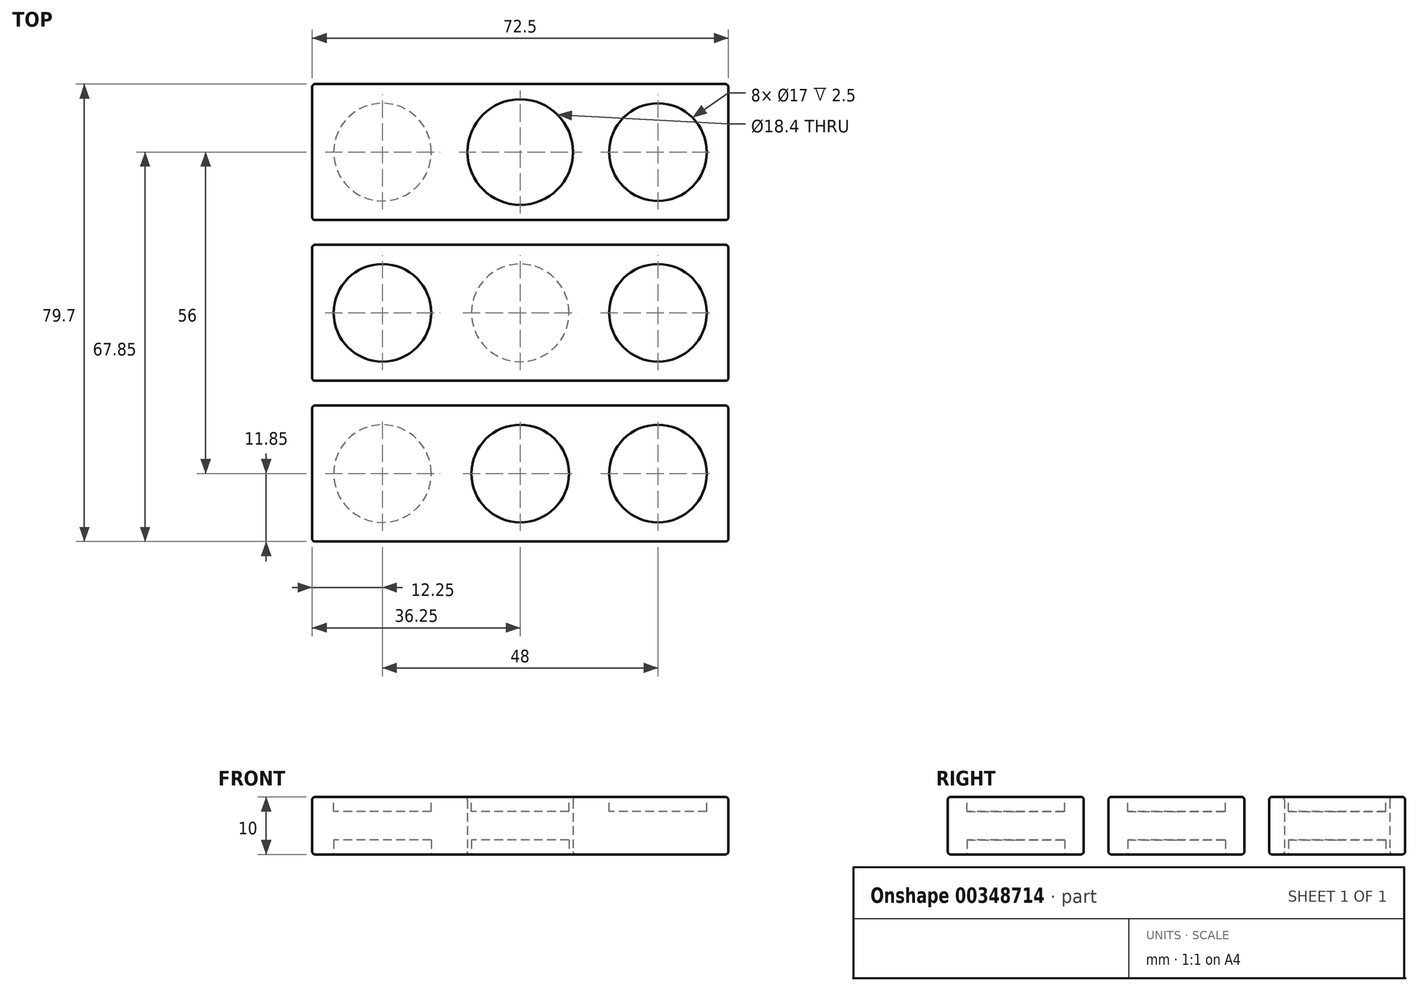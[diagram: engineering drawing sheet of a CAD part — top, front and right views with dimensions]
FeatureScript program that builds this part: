
annotation { "Feature Type Name" : "Feature", "Feature Type Description" : "" }
export const myFeature = defineFeature(function(context is Context, id is Id, definition is map)
    precondition{}
    {
        {
            var Q0;
            Q0=qCreatedBy(makeId("Top.planeOp"),FACE);
            var sketch = newSketch(context, id + "F0", { "sketchPlane" : qUnion([Q0])});
            skLineSegment(sketch, "E0", {"start": v(0, 0) * mm, "end": v(0, -99.1) * mm, "construction": true});
            skLineSegment(sketch, "E1.bottom", {"start": v(0, 0) * mm, "end": v(72.5, 0) * mm});
            skLineSegment(sketch, "E1.top", {"start": v(0, -23.7) * mm, "end": v(72.5, -23.7) * mm});
            skLineSegment(sketch, "E1.left", {"start": v(0, 0) * mm, "end": v(0, -23.7) * mm});
            skLineSegment(sketch, "E1.right", {"start": v(72.5, 0) * mm, "end": v(72.5, -23.7) * mm});
            skLineSegment(sketch, "E2.0.1.0", {"start": v(72.5, -28) * mm, "end": v(72.5, -51.7) * mm});
            skLineSegment(sketch, "E2.0.1.1", {"start": v(0, -51.7) * mm, "end": v(72.5, -51.7) * mm});
            skLineSegment(sketch, "E2.0.1.2", {"start": v(0, -28) * mm, "end": v(72.5, -28) * mm});
            skLineSegment(sketch, "E2.0.1.3", {"start": v(0, -28) * mm, "end": v(0, -51.7) * mm});
            skLineSegment(sketch, "E2.0.2.0", {"start": v(72.5, -56) * mm, "end": v(72.5, -79.7) * mm});
            skLineSegment(sketch, "E2.0.2.1", {"start": v(0, -79.7) * mm, "end": v(72.5, -79.7) * mm});
            skLineSegment(sketch, "E2.0.2.2", {"start": v(0, -56) * mm, "end": v(72.5, -56) * mm});
            skLineSegment(sketch, "E2.0.2.3", {"start": v(0, -56) * mm, "end": v(0, -79.7) * mm});
            skLineSegment(sketch, "E2.0.3.0", {"start": v(72.5, -84) * mm, "end": v(72.5, -107.7) * mm});
            skLineSegment(sketch, "E2.0.3.1", {"start": v(0, -107.7) * mm, "end": v(72.5, -107.7) * mm});
            skLineSegment(sketch, "E2.0.3.2", {"start": v(0, -84) * mm, "end": v(72.5, -84) * mm});
            skLineSegment(sketch, "E2.0.3.3", {"start": v(0, -84) * mm, "end": v(0, -107.7) * mm});
            skLineSegment(sketch, "E2.0.4.0", {"start": v(72.5, -112) * mm, "end": v(72.5, -135.7) * mm});
            skLineSegment(sketch, "E2.0.4.1", {"start": v(0, -135.7) * mm, "end": v(72.5, -135.7) * mm});
            skLineSegment(sketch, "E2.0.4.2", {"start": v(0, -112) * mm, "end": v(72.5, -112) * mm});
            skLineSegment(sketch, "E2.0.4.3", {"start": v(0, -112) * mm, "end": v(0, -135.7) * mm});
            skLineSegment(sketch, "E2.0.5.0", {"start": v(72.5, -140) * mm, "end": v(72.5, -163.7) * mm});
            skLineSegment(sketch, "E2.0.5.1", {"start": v(0, -163.7) * mm, "end": v(72.5, -163.7) * mm});
            skLineSegment(sketch, "E2.0.5.2", {"start": v(0, -140) * mm, "end": v(72.5, -140) * mm});
            skLineSegment(sketch, "E2.0.5.3", {"start": v(0, -140) * mm, "end": v(0, -163.7) * mm});
            skLineSegment(sketch, "E2.direction1", {"start": v(72.5, -23.7) * mm, "end": v(97.83, -23.7) * mm, "construction": true});
            skLineSegment(sketch, "E2.direction2", {"start": v(72.5, -23.7) * mm, "end": v(72.5, -51.7) * mm, "construction": true});
            skLineSegment(sketch, "E3", {"start": v(0, -11.85) * mm, "end": v(12.25, -11.85) * mm, "construction": true});
            skLineSegment(sketch, "E4", {"start": v(12.25, -11.85) * mm, "end": v(36.25, -11.85) * mm, "construction": true});
            skLineSegment(sketch, "E5", {"start": v(36.25, -11.85) * mm, "end": v(60.25, -11.85) * mm, "construction": true});
            skLineSegment(sketch, "E6", {"start": v(60.25, -11.85) * mm, "end": v(72.5, -11.85) * mm, "construction": true});
            skLineSegment(sketch, "E7", {"start": v(12.25, -11.85) * mm, "end": v(12.25, -182.05) * mm, "construction": true});
            skLineSegment(sketch, "E8", {"start": v(36.25, -11.85) * mm, "end": v(36.25, -186.32) * mm, "construction": true});
            skLineSegment(sketch, "E9", {"start": v(60.25, -11.85) * mm, "end": v(60.25, -189.7) * mm, "construction": true});
            skCircle(sketch, "E10", {"center": v(12.25, -11.85) * mm, "radius": 9.2 * mm});
            skCircle(sketch, "E11", {"center": v(36.25, -11.85) * mm, "radius": 9.2 * mm});
            skLineSegment(sketch, "E12", {"start": v(0, -39.85) * mm, "end": v(72.5, -39.85) * mm, "construction": true});
            skLineSegment(sketch, "E13", {"start": v(0, -67.85) * mm, "end": v(72.5, -67.85) * mm, "construction": true});
            skLineSegment(sketch, "E14", {"start": v(0, -95.85) * mm, "end": v(72.5, -95.85) * mm, "construction": true});
            skLineSegment(sketch, "E15", {"start": v(0, -123.85) * mm, "end": v(72.5, -123.85) * mm, "construction": true});
            skLineSegment(sketch, "E16", {"start": v(0, -151.85) * mm, "end": v(72.5, -151.85) * mm, "construction": true});
            skCircle(sketch, "E17", {"center": v(12.25, -39.85) * mm, "radius": 9.2 * mm});
            skCircle(sketch, "E18", {"center": v(12.25, -67.85) * mm, "radius": 9.2 * mm});
            skCircle(sketch, "E19", {"center": v(36.25, -95.85) * mm, "radius": 9.2 * mm});
            skCircle(sketch, "E20", {"center": v(36.25, -39.85) * mm, "radius": 8.5 * mm});
            skCircle(sketch, "E21", {"center": v(36.25, -67.85) * mm, "radius": 8.5 * mm});
            skCircle(sketch, "E22", {"center": v(12.25, -95.85) * mm, "radius": 8.5 * mm});
            skCircle(sketch, "E23", {"center": v(36.25, -123.85) * mm, "radius": 8.5 * mm});
            skCircle(sketch, "E24", {"center": v(12.25, -151.85) * mm, "radius": 8.5 * mm});
            skSolve(sketch);
        }
        {
            var Q0;
            Q0=makeQuery(id+"F0.imprint","IMPRINT",FACE,{"disambiguationData":[TD([[makeQuery(id+"F0.imprint","IMPRINT",EDGE,{"derivedFrom":sQuery(id+"F0.wireOp",EDGE,"E1.bottom")}),-1.0]])]});
            var Q1;
            Q1=makeQuery(id+"F0.imprint","IMPRINT",FACE,{"disambiguationData":[TD([[makeQuery(id+"F0.imprint","IMPRINT",EDGE,{"derivedFrom":sQuery(id+"F0.wireOp",EDGE,"E2.0.1.0")}),-1.0]])]});
            var Q2;
            Q2=makeQuery(id+"F0.imprint","IMPRINT",FACE,{"disambiguationData":[TD([[makeQuery(id+"F0.imprint","IMPRINT",EDGE,{"derivedFrom":sQuery(id+"F0.wireOp",EDGE,"E2.0.2.0")}),-1.0]])]});
            var Q3;
            Q3=makeQuery(id+"F0.imprint","IMPRINT",FACE,{"disambiguationData":[TD([[makeQuery(id+"F0.imprint","IMPRINT",EDGE,{"derivedFrom":sQuery(id+"F0.wireOp",EDGE,"E2.0.3.0")}),-1.0]])]});
            var Q4;
            Q4=makeQuery(id+"F0.imprint","IMPRINT",FACE,{"disambiguationData":[TD([[makeQuery(id+"F0.imprint","IMPRINT",EDGE,{"derivedFrom":sQuery(id+"F0.wireOp",EDGE,"E2.0.4.0")}),-1.0]])]});
            var Q5;
            Q5=makeQuery(id+"F0.imprint","IMPRINT",FACE,{"disambiguationData":[TD([[makeQuery(id+"F0.imprint","IMPRINT",EDGE,{"derivedFrom":sQuery(id+"F0.wireOp",EDGE,"E2.0.5.0")}),-1.0]])]});
            var Q6;
            Q6=makeQuery(id+"F0.imprint","IMPRINT",FACE,{"disambiguationData":[TD([[makeQuery(id+"F0.imprint","IMPRINT",EDGE,{"derivedFrom":sQuery(id+"F0.wireOp",EDGE,"E23")}),1.0]])]});
            var Q7;
            Q7=makeQuery(id+"F0.imprint","IMPRINT",FACE,{"disambiguationData":[TD([[makeQuery(id+"F0.imprint","IMPRINT",EDGE,{"derivedFrom":sQuery(id+"F0.wireOp",EDGE,"E24")}),1.0]])]});
            var Q8;
            Q8=makeQuery(id+"F0.imprint","IMPRINT",FACE,{"disambiguationData":[TD([[makeQuery(id+"F0.imprint","IMPRINT",EDGE,{"derivedFrom":sQuery(id+"F0.wireOp",EDGE,"E21")}),1.0]])]});
            var Q9;
            Q9=makeQuery(id+"F0.imprint","IMPRINT",FACE,{"disambiguationData":[TD([[makeQuery(id+"F0.imprint","IMPRINT",EDGE,{"derivedFrom":sQuery(id+"F0.wireOp",EDGE,"E20")}),1.0]])]});
            var Q10;
            Q10=makeQuery(id+"F0.imprint","IMPRINT",FACE,{"disambiguationData":[TD([[makeQuery(id+"F0.imprint","IMPRINT",EDGE,{"derivedFrom":sQuery(id+"F0.wireOp",EDGE,"E22")}),1.0]])]});
            extrude(context, id + "F1", {"entities" : qUnion([Q0, Q1, Q2, Q3, Q4, Q5, Q6, Q7, Q8, Q9, Q10]), "depth" : 10 * mm});
        }
        {
            var Q0;
            Q0=makeQuery(id+"F0.imprint","IMPRINT",FACE,{"disambiguationData":[TD([[makeQuery(id+"F0.imprint","IMPRINT",EDGE,{"derivedFrom":sQuery(id+"F0.wireOp",EDGE,"E24")}),1.0]])]});
            var Q1;
            Q1=makeQuery(id+"F0.imprint","IMPRINT",FACE,{"disambiguationData":[TD([[makeQuery(id+"F0.imprint","IMPRINT",EDGE,{"derivedFrom":sQuery(id+"F0.wireOp",EDGE,"E23")}),1.0]])]});
            var Q2;
            Q2=makeQuery(id+"F0.imprint","IMPRINT",FACE,{"disambiguationData":[TD([[makeQuery(id+"F0.imprint","IMPRINT",EDGE,{"derivedFrom":sQuery(id+"F0.wireOp",EDGE,"E22")}),1.0]])]});
            var Q3;
            Q3=makeQuery(id+"F0.imprint","IMPRINT",FACE,{"disambiguationData":[TD([[makeQuery(id+"F0.imprint","IMPRINT",EDGE,{"derivedFrom":sQuery(id+"F0.wireOp",EDGE,"E21")}),1.0]])]});
            var Q4;
            Q4=makeQuery(id+"F0.imprint","IMPRINT",FACE,{"disambiguationData":[TD([[makeQuery(id+"F0.imprint","IMPRINT",EDGE,{"derivedFrom":sQuery(id+"F0.wireOp",EDGE,"E20")}),1.0]])]});
            extrude(context, id + "F2", {"entities" : qUnion([Q0, Q1, Q2, Q3, Q4]), "operationType" : NewBodyOperationType.REMOVE, "depth" : 2.5 * mm});
        }
        {
            var Q0;
            Q0=makeQuery(id+"F1.opExtrude","CAP_FACE",FACE,{"disambiguationData":[OSD([sQuery(id+"F0.wireOp",EDGE,"E2.0.5.0"),sQuery(id+"F0.wireOp",EDGE,"E2.0.5.1"),sQuery(id+"F0.wireOp",EDGE,"E2.0.5.2"),sQuery(id+"F0.wireOp",EDGE,"E2.0.5.3")])],"isStart":false});
            var sketch = newSketch(context, id + "F3", { "sketchPlane" : qUnion([Q0])});
            skCircle(sketch, "E25", {"center": v(60.25, -11.85) * mm, "radius": 8.5 * mm});
            skCircle(sketch, "E26", {"center": v(60.25, -39.85) * mm, "radius": 8.5 * mm});
            skCircle(sketch, "E27", {"center": v(60.25, -67.85) * mm, "radius": 8.5 * mm});
            skCircle(sketch, "E28", {"center": v(60.25, -95.85) * mm, "radius": 8.5 * mm});
            skCircle(sketch, "E29", {"center": v(60.25, -123.85) * mm, "radius": 8.5 * mm});
            skCircle(sketch, "E30", {"center": v(12.25, -123.85) * mm, "radius": 8.5 * mm});
            skCircle(sketch, "E31", {"center": v(36.25, -151.85) * mm, "radius": 8.5 * mm});
            skCircle(sketch, "E32", {"center": v(60.25, -151.85) * mm, "radius": 8.5 * mm});
            skLineSegment(sketch, "E33", {"start": v(36.25, -163.7) * mm, "end": v(36.25, 0) * mm, "construction": true});
            skPoint(sketch, "E34.startSnap0", {"position": v(0, -151.85) * mm});
            skLineSegment(sketch, "E35", {"start": v(0, -151.85) * mm, "end": v(0, -125.8) * mm, "construction": true});
            skLineSegment(sketch, "E36", {"start": v(0, -151.85) * mm, "end": v(12.25, -151.85) * mm, "construction": true});
            skLineSegment(sketch, "E37", {"start": v(12.25, -151.85) * mm, "end": v(36.25, -151.85) * mm, "construction": true});
            skLineSegment(sketch, "E38", {"start": v(36.25, -151.85) * mm, "end": v(60.25, -151.85) * mm, "construction": true});
            skLineSegment(sketch, "E39", {"start": v(60.25, -151.85) * mm, "end": v(72.5, -151.85) * mm, "construction": true});
            skLineSegment(sketch, "E40.0.1.0", {"start": v(0, -123.85) * mm, "end": v(12.25, -123.85) * mm, "construction": true});
            skLineSegment(sketch, "E40.0.1.1", {"start": v(12.25, -123.85) * mm, "end": v(36.25, -123.85) * mm, "construction": true});
            skLineSegment(sketch, "E40.0.1.2", {"start": v(36.25, -123.85) * mm, "end": v(60.25, -123.85) * mm, "construction": true});
            skLineSegment(sketch, "E40.0.1.3", {"start": v(60.25, -123.85) * mm, "end": v(72.5, -123.85) * mm, "construction": true});
            skLineSegment(sketch, "E40.0.2.0", {"start": v(0, -95.85) * mm, "end": v(12.25, -95.85) * mm, "construction": true});
            skLineSegment(sketch, "E40.0.2.1", {"start": v(12.25, -95.85) * mm, "end": v(36.25, -95.85) * mm, "construction": true});
            skLineSegment(sketch, "E40.0.2.2", {"start": v(36.25, -95.85) * mm, "end": v(60.25, -95.85) * mm, "construction": true});
            skLineSegment(sketch, "E40.0.2.3", {"start": v(60.25, -95.85) * mm, "end": v(72.5, -95.85) * mm, "construction": true});
            skLineSegment(sketch, "E40.0.3.0", {"start": v(0, -67.85) * mm, "end": v(12.25, -67.85) * mm, "construction": true});
            skLineSegment(sketch, "E40.0.3.1", {"start": v(12.25, -67.85) * mm, "end": v(36.25, -67.85) * mm, "construction": true});
            skLineSegment(sketch, "E40.0.3.2", {"start": v(36.25, -67.85) * mm, "end": v(60.25, -67.85) * mm, "construction": true});
            skLineSegment(sketch, "E40.0.3.3", {"start": v(60.25, -67.85) * mm, "end": v(72.5, -67.85) * mm, "construction": true});
            skLineSegment(sketch, "E40.0.4.0", {"start": v(0, -39.85) * mm, "end": v(12.25, -39.85) * mm, "construction": true});
            skLineSegment(sketch, "E40.0.4.1", {"start": v(12.25, -39.85) * mm, "end": v(36.25, -39.85) * mm, "construction": true});
            skLineSegment(sketch, "E40.0.4.2", {"start": v(36.25, -39.85) * mm, "end": v(60.25, -39.85) * mm, "construction": true});
            skLineSegment(sketch, "E40.0.4.3", {"start": v(60.25, -39.85) * mm, "end": v(72.5, -39.85) * mm, "construction": true});
            skLineSegment(sketch, "E40.0.5.0", {"start": v(0, -11.85) * mm, "end": v(12.25, -11.85) * mm, "construction": true});
            skLineSegment(sketch, "E40.0.5.1", {"start": v(12.25, -11.85) * mm, "end": v(36.25, -11.85) * mm, "construction": true});
            skLineSegment(sketch, "E40.0.5.2", {"start": v(36.25, -11.85) * mm, "end": v(60.25, -11.85) * mm, "construction": true});
            skLineSegment(sketch, "E40.0.5.3", {"start": v(60.25, -11.85) * mm, "end": v(72.5, -11.85) * mm, "construction": true});
            skLineSegment(sketch, "E40.direction1", {"start": v(0, -151.85) * mm, "end": v(25, -151.85) * mm, "construction": true});
            skLineSegment(sketch, "E40.direction2", {"start": v(0, -151.85) * mm, "end": v(0, -123.85) * mm, "construction": true});
            skSolve(sketch);
        }
        {
            var Q0;
            Q0=makeQuery(id+"F3.imprint","IMPRINT",FACE,{"disambiguationData":[TD([[makeQuery(id+"F3.imprint","IMPRINT",EDGE,{"derivedFrom":sQuery(id+"F3.wireOp",EDGE,"E30")}),1.0]])]});
            var Q1;
            Q1=makeQuery(id+"F3.imprint","IMPRINT",FACE,{"disambiguationData":[TD([[makeQuery(id+"F3.imprint","IMPRINT",EDGE,{"derivedFrom":sQuery(id+"F3.wireOp",EDGE,"E31")}),1.0]])]});
            var Q2;
            Q2=makeQuery(id+"F3.imprint","IMPRINT",FACE,{"disambiguationData":[TD([[makeQuery(id+"F3.imprint","IMPRINT",EDGE,{"derivedFrom":sQuery(id+"F3.wireOp",EDGE,"E32")}),1.0]])]});
            var Q3;
            Q3=makeQuery(id+"F3.imprint","IMPRINT",FACE,{"disambiguationData":[TD([[makeQuery(id+"F3.imprint","IMPRINT",EDGE,{"derivedFrom":sQuery(id+"F3.wireOp",EDGE,"E29")}),1.0]])]});
            var Q4;
            Q4=makeQuery(id+"F3.imprint","IMPRINT",FACE,{"disambiguationData":[TD([[makeQuery(id+"F3.imprint","IMPRINT",EDGE,{"derivedFrom":sQuery(id+"F3.wireOp",EDGE,"E28")}),1.0]])]});
            var Q5;
            Q5=makeQuery(id+"F3.imprint","IMPRINT",FACE,{"disambiguationData":[TD([[makeQuery(id+"F3.imprint","IMPRINT",EDGE,{"derivedFrom":sQuery(id+"F3.wireOp",EDGE,"E27")}),1.0]])]});
            var Q6;
            Q6=makeQuery(id+"F3.imprint","IMPRINT",FACE,{"disambiguationData":[TD([[makeQuery(id+"F3.imprint","IMPRINT",EDGE,{"derivedFrom":sQuery(id+"F3.wireOp",EDGE,"E26")}),1.0]])]});
            var Q7;
            Q7=makeQuery(id+"F3.imprint","IMPRINT",FACE,{"disambiguationData":[TD([[makeQuery(id+"F3.imprint","IMPRINT",EDGE,{"derivedFrom":sQuery(id+"F3.wireOp",EDGE,"E25")}),1.0]])]});
            extrude(context, id + "F4", {"entities" : qUnion([Q0, Q1, Q2, Q3, Q4, Q5, Q6, Q7]), "operationType" : NewBodyOperationType.REMOVE, "oppositeDirection" : true, "depth" : 2.5 * mm});
        }
        {
            var Q0;
            Q0=makeQuery(id+"F1.opExtrude","SWEPT_FACE",FACE,{"disambiguationData":[OSD([sQuery(id+"F0.wireOp",EDGE,"E2.0.5.1")])]});
            var Q1;
            Q1=makeQuery(id+"F1.opExtrude","SWEPT_FACE",FACE,{"disambiguationData":[OSD([sQuery(id+"F0.wireOp",EDGE,"E2.0.5.0")])]});
            var Q2;
            Q2=makeQuery(id+"F1.opExtrude","SWEPT_FACE",FACE,{"disambiguationData":[OSD([sQuery(id+"F0.wireOp",EDGE,"E2.0.4.0")])]});
            var Q3;
            Q3=makeQuery(id+"F1.opExtrude","SWEPT_FACE",FACE,{"disambiguationData":[OSD([sQuery(id+"F0.wireOp",EDGE,"E2.0.3.0")])]});
            var Q4;
            Q4=makeQuery(id+"F1.opExtrude","SWEPT_FACE",FACE,{"disambiguationData":[OSD([sQuery(id+"F0.wireOp",EDGE,"E2.0.2.0")])]});
            var Q5;
            Q5=makeQuery(id+"F1.opExtrude","SWEPT_FACE",FACE,{"disambiguationData":[OSD([sQuery(id+"F0.wireOp",EDGE,"E2.0.1.0")])]});
            var Q6;
            Q6=makeQuery(id+"F1.opExtrude","SWEPT_FACE",FACE,{"disambiguationData":[OSD([sQuery(id+"F0.wireOp",EDGE,"E1.right")])]});
            var Q7;
            Q7=makeQuery(id+"F1.opExtrude","SWEPT_FACE",FACE,{"disambiguationData":[OSD([sQuery(id+"F0.wireOp",EDGE,"E1.bottom")])]});
            var Q8;
            Q8=makeQuery(id+"F1.opExtrude","SWEPT_FACE",FACE,{"disambiguationData":[OSD([sQuery(id+"F0.wireOp",EDGE,"E1.left")])]});
            var Q9;
            Q9=makeQuery(id+"F1.opExtrude","SWEPT_FACE",FACE,{"disambiguationData":[OSD([sQuery(id+"F0.wireOp",EDGE,"E2.0.1.3")])]});
            var Q10;
            Q10=makeQuery(id+"F1.opExtrude","SWEPT_FACE",FACE,{"disambiguationData":[OSD([sQuery(id+"F0.wireOp",EDGE,"E2.0.2.3")])]});
            var Q11;
            Q11=makeQuery(id+"F1.opExtrude","SWEPT_FACE",FACE,{"disambiguationData":[OSD([sQuery(id+"F0.wireOp",EDGE,"E2.0.3.3")])]});
            var Q12;
            Q12=makeQuery(id+"F1.opExtrude","SWEPT_FACE",FACE,{"disambiguationData":[OSD([sQuery(id+"F0.wireOp",EDGE,"E2.0.4.3")])]});
            var Q13;
            Q13=makeQuery(id+"F1.opExtrude","SWEPT_FACE",FACE,{"disambiguationData":[OSD([sQuery(id+"F0.wireOp",EDGE,"E2.0.5.3")])]});
            var Q14;
            Q14=makeQuery(id+"F1.opExtrude","SWEPT_FACE",FACE,{"disambiguationData":[OSD([sQuery(id+"F0.wireOp",EDGE,"E2.0.5.2")])]});
            var Q15;
            Q15=makeQuery(id+"F1.opExtrude","SWEPT_FACE",FACE,{"disambiguationData":[OSD([sQuery(id+"F0.wireOp",EDGE,"E2.0.4.2")])]});
            var Q16;
            Q16=makeQuery(id+"F1.opExtrude","SWEPT_FACE",FACE,{"disambiguationData":[OSD([sQuery(id+"F0.wireOp",EDGE,"E2.0.3.2")])]});
            var Q17;
            Q17=makeQuery(id+"F1.opExtrude","SWEPT_FACE",FACE,{"disambiguationData":[OSD([sQuery(id+"F0.wireOp",EDGE,"E2.0.2.2")])]});
            var Q18;
            Q18=makeQuery(id+"F1.opExtrude","SWEPT_FACE",FACE,{"disambiguationData":[OSD([sQuery(id+"F0.wireOp",EDGE,"E2.0.1.2")])]});
            var Q19;
            Q19=makeQuery(id+"F1.opExtrude","SWEPT_FACE",FACE,{"disambiguationData":[OSD([sQuery(id+"F0.wireOp",EDGE,"E1.top")])]});
            var Q20;
            Q20=makeQuery(id+"F1.opExtrude","SWEPT_FACE",FACE,{"disambiguationData":[OSD([sQuery(id+"F0.wireOp",EDGE,"E2.0.1.1")])]});
            var Q21;
            Q21=makeQuery(id+"F1.opExtrude","SWEPT_FACE",FACE,{"disambiguationData":[OSD([sQuery(id+"F0.wireOp",EDGE,"E2.0.2.1")])]});
            var Q22;
            Q22=makeQuery(id+"F1.opExtrude","SWEPT_FACE",FACE,{"disambiguationData":[OSD([sQuery(id+"F0.wireOp",EDGE,"E2.0.3.1")])]});
            var Q23;
            Q23=makeQuery(id+"F1.opExtrude","SWEPT_FACE",FACE,{"disambiguationData":[OSD([sQuery(id+"F0.wireOp",EDGE,"E2.0.4.1")])]});
            fillet(context, id + "F5", {"entities" : qUnion([Q0, Q1, Q2, Q3, Q4, Q5, Q6, Q7, Q8, Q9, Q10, Q11, Q12, Q13, Q14, Q15, Q16, Q17, Q18, Q19, Q20, Q21, Q22, Q23]), "radius" : 0.5 * mm, "tangentPropagation" : true, "allowEdgeOverflow" : false});
        }
        {
            var Q0;
            Q0=makeQuery(id+"F1.opExtrude","SWEPT_FACE",FACE,{"disambiguationData":[OSD([sQuery(id+"F0.wireOp",EDGE,"E17")])]});
            var Q1;
            Q1=makeQuery(id+"F1.opExtrude","SWEPT_FACE",FACE,{"disambiguationData":[OSD([sQuery(id+"F0.wireOp",EDGE,"E10")])]});
            var Q2;
            Q2=makeQuery(id+"F1.opExtrude","SWEPT_FACE",FACE,{"disambiguationData":[OSD([sQuery(id+"F0.wireOp",EDGE,"E11")])]});
            var Q3;
            Q3=makeQuery(id+"F1.opExtrude","SWEPT_FACE",FACE,{"disambiguationData":[OSD([sQuery(id+"F0.wireOp",EDGE,"E18")])]});
            var Q4;
            Q4=makeQuery(id+"F1.opExtrude","SWEPT_FACE",FACE,{"disambiguationData":[OSD([sQuery(id+"F0.wireOp",EDGE,"E19")])]});
            fillet(context, id + "F6", {"entities" : qUnion([Q0, Q1, Q2, Q3, Q4]), "radius" : 0.5 * mm, "tangentPropagation" : true, "allowEdgeOverflow" : false});
        }
        {
            var Q0;
            Q0=makeQuery(id+"F1.opExtrude","SWEPT_BODY",BODY,{"disambiguationData":[OSD([sQuery(id+"F0.wireOp",EDGE,"E1.bottom"),sQuery(id+"F0.wireOp",EDGE,"E1.top"),sQuery(id+"F0.wireOp",EDGE,"E1.left"),sQuery(id+"F0.wireOp",EDGE,"E1.right"),sQuery(id+"F0.wireOp",EDGE,"E10"),sQuery(id+"F0.wireOp",EDGE,"E11")])]});
            var Q1;
            Q1=makeQuery(id+"F1.opExtrude","SWEPT_BODY",BODY,{"disambiguationData":[OSD([sQuery(id+"F0.wireOp",EDGE,"E2.0.1.0"),sQuery(id+"F0.wireOp",EDGE,"E2.0.1.1"),sQuery(id+"F0.wireOp",EDGE,"E2.0.1.2"),sQuery(id+"F0.wireOp",EDGE,"E2.0.1.3"),sQuery(id+"F0.wireOp",EDGE,"E17")])]});
            var Q2;
            Q2=makeQuery(id+"F1.opExtrude","SWEPT_BODY",BODY,{"disambiguationData":[OSD([sQuery(id+"F0.wireOp",EDGE,"E2.0.2.0"),sQuery(id+"F0.wireOp",EDGE,"E2.0.2.1"),sQuery(id+"F0.wireOp",EDGE,"E2.0.2.2"),sQuery(id+"F0.wireOp",EDGE,"E2.0.2.3"),sQuery(id+"F0.wireOp",EDGE,"E18")])]});
            deleteBodies(context, id + "F7", {"entities" : qUnion([Q0, Q1, Q2])});
        }
    });
